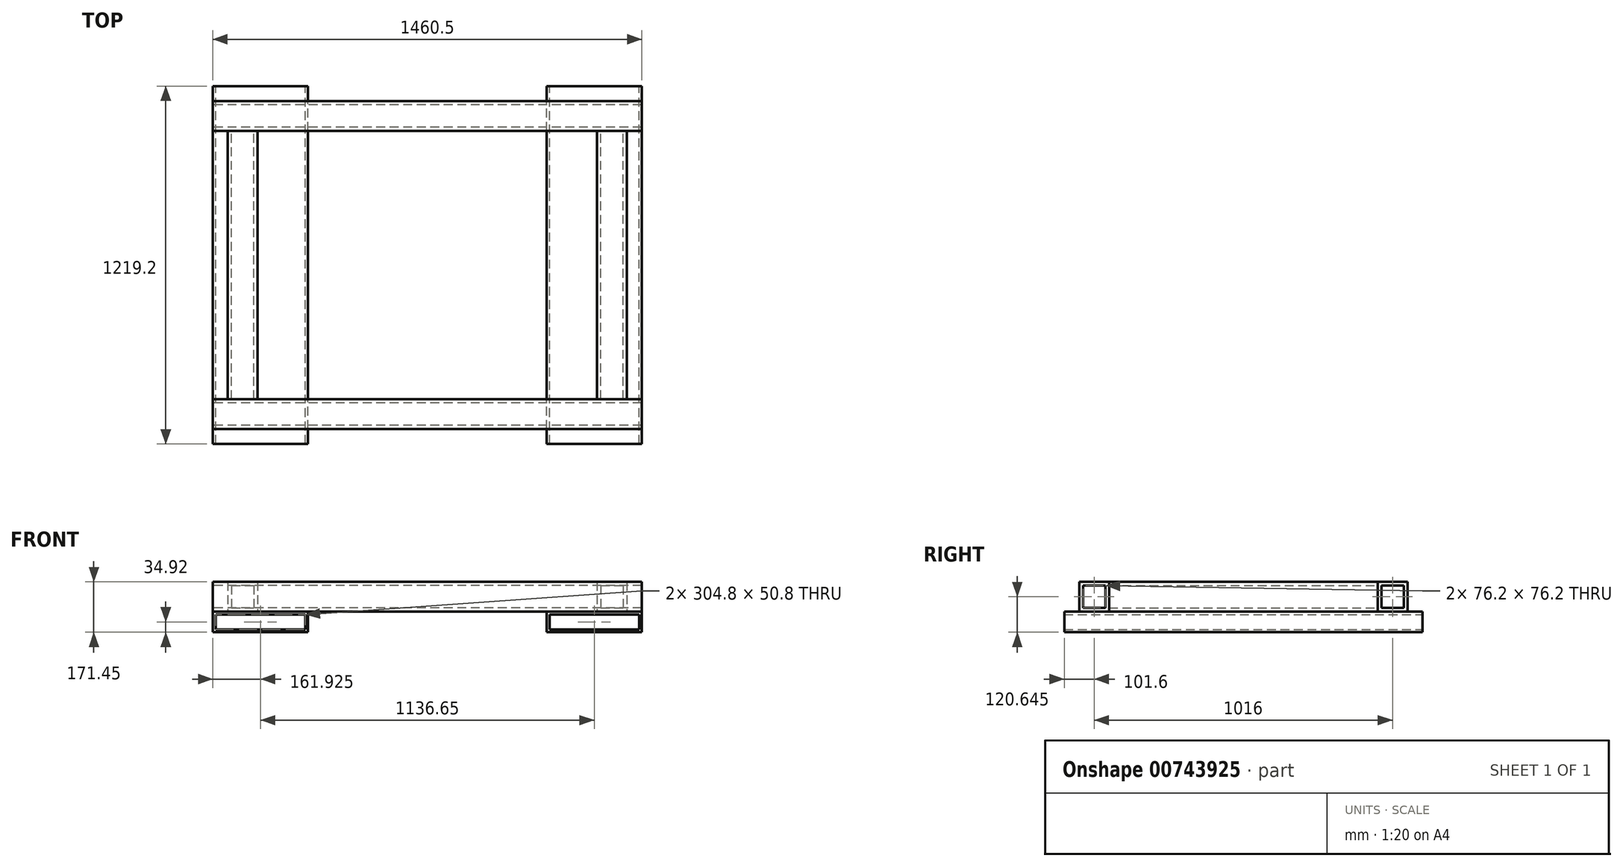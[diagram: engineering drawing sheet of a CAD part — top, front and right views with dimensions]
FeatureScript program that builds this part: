
annotation { "Feature Type Name" : "Feature", "Feature Type Description" : "" }
export const myFeature = defineFeature(function(context is Context, id is Id, definition is map)
    precondition{}
    {
        {
            var Q0;
            Q0=qCreatedBy(makeId("Front.planeOp"),FACE);
            var sketch = newSketch(context, id + "F0", { "sketchPlane" : qUnion([Q0])});
            skLineSegment(sketch, "E0.bottom", {"start": v(-720.73, 25.4) * mm, "end": v(-415.93, 25.4) * mm});
            skLineSegment(sketch, "E0.top", {"start": v(-720.73, -25.4) * mm, "end": v(-415.93, -25.4) * mm});
            skLineSegment(sketch, "E0.left", {"start": v(-720.73, 25.4) * mm, "end": v(-720.73, -25.4) * mm});
            skLineSegment(sketch, "E0.right", {"start": v(-415.93, 25.4) * mm, "end": v(-415.93, -25.4) * mm});
            skLineSegment(sketch, "E1.bottom", {"start": v(415.93, 25.4) * mm, "end": v(720.73, 25.4) * mm});
            skLineSegment(sketch, "E1.top", {"start": v(415.93, -25.4) * mm, "end": v(720.73, -25.4) * mm});
            skLineSegment(sketch, "E1.left", {"start": v(415.93, 25.4) * mm, "end": v(415.93, -25.4) * mm});
            skLineSegment(sketch, "E1.right", {"start": v(720.73, 25.4) * mm, "end": v(720.73, -25.4) * mm});
            skLineSegment(sketch, "E2.0", {"start": v(-730.25, 34.93) * mm, "end": v(-406.4, 34.93) * mm});
            skLineSegment(sketch, "E2.1", {"start": v(-730.25, 34.93) * mm, "end": v(-730.25, -34.93) * mm});
            skLineSegment(sketch, "E2.2", {"start": v(-730.25, -34.93) * mm, "end": v(-406.4, -34.93) * mm});
            skLineSegment(sketch, "E2.3", {"start": v(-406.4, 34.93) * mm, "end": v(-406.4, -34.93) * mm});
            skLineSegment(sketch, "E3.0", {"start": v(406.4, 34.93) * mm, "end": v(730.25, 34.93) * mm});
            skLineSegment(sketch, "E3.1", {"start": v(406.4, 34.93) * mm, "end": v(406.4, -34.92) * mm});
            skLineSegment(sketch, "E3.2", {"start": v(406.4, -34.92) * mm, "end": v(730.25, -34.92) * mm});
            skLineSegment(sketch, "E3.3", {"start": v(730.25, 34.93) * mm, "end": v(730.25, -34.92) * mm});
            skSolve(sketch);
        }
        {
            var Q0;
            Q0=makeQuery(id+"F0.imprint","IMPRINT",FACE,{"disambiguationData":[TD([[makeQuery(id+"F0.imprint","IMPRINT",EDGE,{"derivedFrom":sQuery(id+"F0.wireOp",EDGE,"E0.bottom")}),1.0]])]});
            var Q1;
            Q1=makeQuery(id+"F0.imprint","IMPRINT",FACE,{"disambiguationData":[TD([[makeQuery(id+"F0.imprint","IMPRINT",EDGE,{"derivedFrom":sQuery(id+"F0.wireOp",EDGE,"E1.bottom")}),1.0]])]});
            extrude(context, id + "F1", {"entities" : qUnion([Q0, Q1]), "endBound" : BoundingType.SYMMETRIC, "depth" : 1219.2 * mm, "offsetDistance" : 25.4 * mm});
        }
        {
            var Q0;
            Q0=makeQuery(id+"F1.opExtrude","SWEPT_FACE",FACE,{"disambiguationData":[OSD([sQuery(id+"F0.wireOp",EDGE,"E2.1")])]});
            var sketch = newSketch(context, id + "F2", { "sketchPlane" : qUnion([Q0])});
            skLineSegment(sketch, "E4.bottom", {"start": v(457.2, 136.53) * mm, "end": v(558.8, 136.53) * mm});
            skLineSegment(sketch, "E4.top", {"start": v(457.2, 34.93) * mm, "end": v(609.6, 34.93) * mm});
            skLineSegment(sketch, "E4.left", {"start": v(457.2, 136.53) * mm, "end": v(457.2, 34.93) * mm});
            skLineSegment(sketch, "E4.right", {"start": v(558.8, 136.53) * mm, "end": v(558.8, 34.93) * mm});
            skLineSegment(sketch, "E5.bottom", {"start": v(-558.8, 136.53) * mm, "end": v(-457.2, 136.53) * mm});
            skLineSegment(sketch, "E5.top", {"start": v(-558.8, 34.93) * mm, "end": v(-457.2, 34.93) * mm});
            skLineSegment(sketch, "E5.left", {"start": v(-558.8, 136.53) * mm, "end": v(-558.8, 34.93) * mm});
            skLineSegment(sketch, "E5.right", {"start": v(-457.2, 136.53) * mm, "end": v(-457.2, 34.93) * mm});
            skLineSegment(sketch, "E6.0", {"start": v(-546.1, 123.83) * mm, "end": v(-469.9, 123.83) * mm});
            skLineSegment(sketch, "E6.1", {"start": v(-546.1, 123.83) * mm, "end": v(-546.1, 47.63) * mm});
            skLineSegment(sketch, "E6.2", {"start": v(-546.1, 47.63) * mm, "end": v(-469.9, 47.63) * mm});
            skLineSegment(sketch, "E6.3", {"start": v(-469.9, 123.83) * mm, "end": v(-469.9, 47.63) * mm});
            skLineSegment(sketch, "E7.0", {"start": v(469.9, 123.83) * mm, "end": v(546.1, 123.83) * mm});
            skLineSegment(sketch, "E7.1", {"start": v(469.9, 123.83) * mm, "end": v(469.9, 47.63) * mm});
            skLineSegment(sketch, "E7.2", {"start": v(469.9, 47.63) * mm, "end": v(546.1, 47.63) * mm});
            skLineSegment(sketch, "E7.3", {"start": v(546.1, 123.83) * mm, "end": v(546.1, 47.63) * mm});
            skSolve(sketch);
        }
        {
            var Q0;
            Q0=makeQuery(id+"F2.imprint","IMPRINT",FACE,{"disambiguationData":[TD([[makeQuery(id+"F2.imprint","IMPRINT",EDGE,{"derivedFrom":sQuery(id+"F2.wireOp",EDGE,"E4.bottom")}),-1.0]])]});
            var Q1;
            Q1=makeQuery(id+"F2.imprint","IMPRINT",FACE,{"disambiguationData":[TD([[makeQuery(id+"F2.imprint","IMPRINT",EDGE,{"derivedFrom":sQuery(id+"F2.wireOp",EDGE,"E5.bottom")}),-1.0]])]});
            extrude(context, id + "F3", {"entities" : qUnion([Q0, Q1]), "oppositeDirection" : true, "depth" : 1460.5 * mm, "offsetDistance" : 25.4 * mm});
        }
        {
            var Q0;
            Q0=makeQuery(id+"F3.opExtrude","SWEPT_FACE",FACE,{"disambiguationData":[OSD([sQuery(id+"F2.wireOp",EDGE,"E5.right")])]});
            var sketch = newSketch(context, id + "F4", { "sketchPlane" : qUnion([Q0])});
            skLineSegment(sketch, "E8.bottom", {"start": v(-679.45, 136.53) * mm, "end": v(-577.85, 136.53) * mm});
            skLineSegment(sketch, "E8.top", {"start": v(-679.45, 34.93) * mm, "end": v(-577.85, 34.93) * mm});
            skLineSegment(sketch, "E8.left", {"start": v(-679.45, 136.53) * mm, "end": v(-679.45, 34.93) * mm});
            skLineSegment(sketch, "E8.right", {"start": v(-577.85, 136.53) * mm, "end": v(-577.85, 34.93) * mm});
            skLineSegment(sketch, "E9.bottom", {"start": v(577.85, 136.53) * mm, "end": v(679.45, 136.53) * mm});
            skLineSegment(sketch, "E9.top", {"start": v(577.85, 34.93) * mm, "end": v(679.45, 34.93) * mm});
            skLineSegment(sketch, "E9.left", {"start": v(577.85, 136.53) * mm, "end": v(577.85, 34.93) * mm});
            skLineSegment(sketch, "E9.right", {"start": v(679.45, 136.53) * mm, "end": v(679.45, 34.93) * mm});
            skLineSegment(sketch, "E10.0", {"start": v(-666.75, 123.83) * mm, "end": v(-590.55, 123.83) * mm});
            skLineSegment(sketch, "E10.1", {"start": v(-666.75, 123.83) * mm, "end": v(-666.75, 47.63) * mm});
            skLineSegment(sketch, "E10.2", {"start": v(-666.75, 47.63) * mm, "end": v(-590.55, 47.63) * mm});
            skLineSegment(sketch, "E10.3", {"start": v(-590.55, 123.83) * mm, "end": v(-590.55, 47.63) * mm});
            skLineSegment(sketch, "E11.0", {"start": v(666.75, 123.83) * mm, "end": v(666.75, 47.63) * mm});
            skLineSegment(sketch, "E11.1", {"start": v(590.55, 123.83) * mm, "end": v(666.75, 123.83) * mm});
            skLineSegment(sketch, "E11.2", {"start": v(590.55, 123.83) * mm, "end": v(590.55, 47.63) * mm});
            skLineSegment(sketch, "E11.3", {"start": v(590.55, 47.63) * mm, "end": v(666.75, 47.63) * mm});
            skSolve(sketch);
        }
        {
            var Q0;
            Q0=makeQuery(id+"F4.imprint","IMPRINT",FACE,{"disambiguationData":[TD([[makeQuery(id+"F4.imprint","IMPRINT",EDGE,{"derivedFrom":sQuery(id+"F4.wireOp",EDGE,"E8.bottom")}),1.0]])]});
            var Q1;
            Q1=makeQuery(id+"F4.imprint","IMPRINT",FACE,{"disambiguationData":[TD([[makeQuery(id+"F4.imprint","IMPRINT",EDGE,{"derivedFrom":sQuery(id+"F4.wireOp",EDGE,"E9.bottom")}),1.0]])]});
            extrude(context, id + "F5", {"entities" : qUnion([Q0, Q1]), "depth" : 914.4 * mm, "offsetDistance" : 25.4 * mm});
        }
    });
